# Revit family: CADS_Vent-Axia_Lo-CarbonSentinelHorizontal200ZMH
name_source: partatom
category: Mechanical Equipment
revit_build: Autodesk Revit 2015 (Build: 20160512_1515(x64)
units: mm (PartAtom-declared; Revit-internal decimal feet)

## types (1)
- 200ZMH
    Apparent Load = 690 VA
    AssetType = Fixed
    C = 200 mm  [stored 0.656168 ft]
    Category = Pr_60_60_36:Heat recovery distribution equipment
    Color = Galvanised Steel
    Description = Lo-Carbon Sentinel Kinetic Horizontal
    DurationUnit = year
    E = 195 mm  [stored 0.639764 ft]
    ExpectedLife = 20
    F = 140 mm  [stored 0.459318 ft]
    Features = Summer By-Pass/Humidistat
    G = 54 mm  [stored 0.177165 ft]
    H = 66 mm  [stored 0.216535 ft]
    I = 168 mm  [stored 0.551181 ft]
    IfcExportAs = IfcAirToAirHeatRecoveryType
    IfcExportType = USERDEFINED
    J = 138 mm  [stored 0.452756 ft]
    K = 143 mm
    Manufacturer = Vent-Axia Limited
    Material = Galvanised Steel
    Model = Kinetic Horizontal 200ZMH
    ModelNumber = 448778
    ModelReference = Kinetic Horizontal 200ZMH
    Name = MVHR Unit
    NominalHeight = 200 mm  [stored 0.656168 ft]
    NominalLength = 849 mm  [stored 2.78543 ft]
    NominalWidth = 570 mm  [stored 1.87008 ft]
    NumberOfPoles = 1
    RatedCurrent = 3 A
    RatedVoltage = 230 V
    Shape = Rectangular
    Size = 570mm x 849mm x 200mm 
570mm x 849mm x 200mm
    SpigotDiameter = 125 mm  [stored 0.410105 ft]
    SpigotLength = 204 mm  [stored 0.669291 ft]
    SpigotWidth = 60 mm  [stored 0.19685 ft]
    Version = 1.0
    WarrantyDurationLabor = 2
    WarrantyDurationMotors = 5
    WarrantyDurationParts = 2
    WarrantyDurationUnit = year

note: [stored X ft] marks values corroborated as IEEE doubles in the binary element streams (Revit-internal decimal feet)

## geometry (parser evidence)
native form markers: Sweep x17
no freeform markers — native parametric forms only
